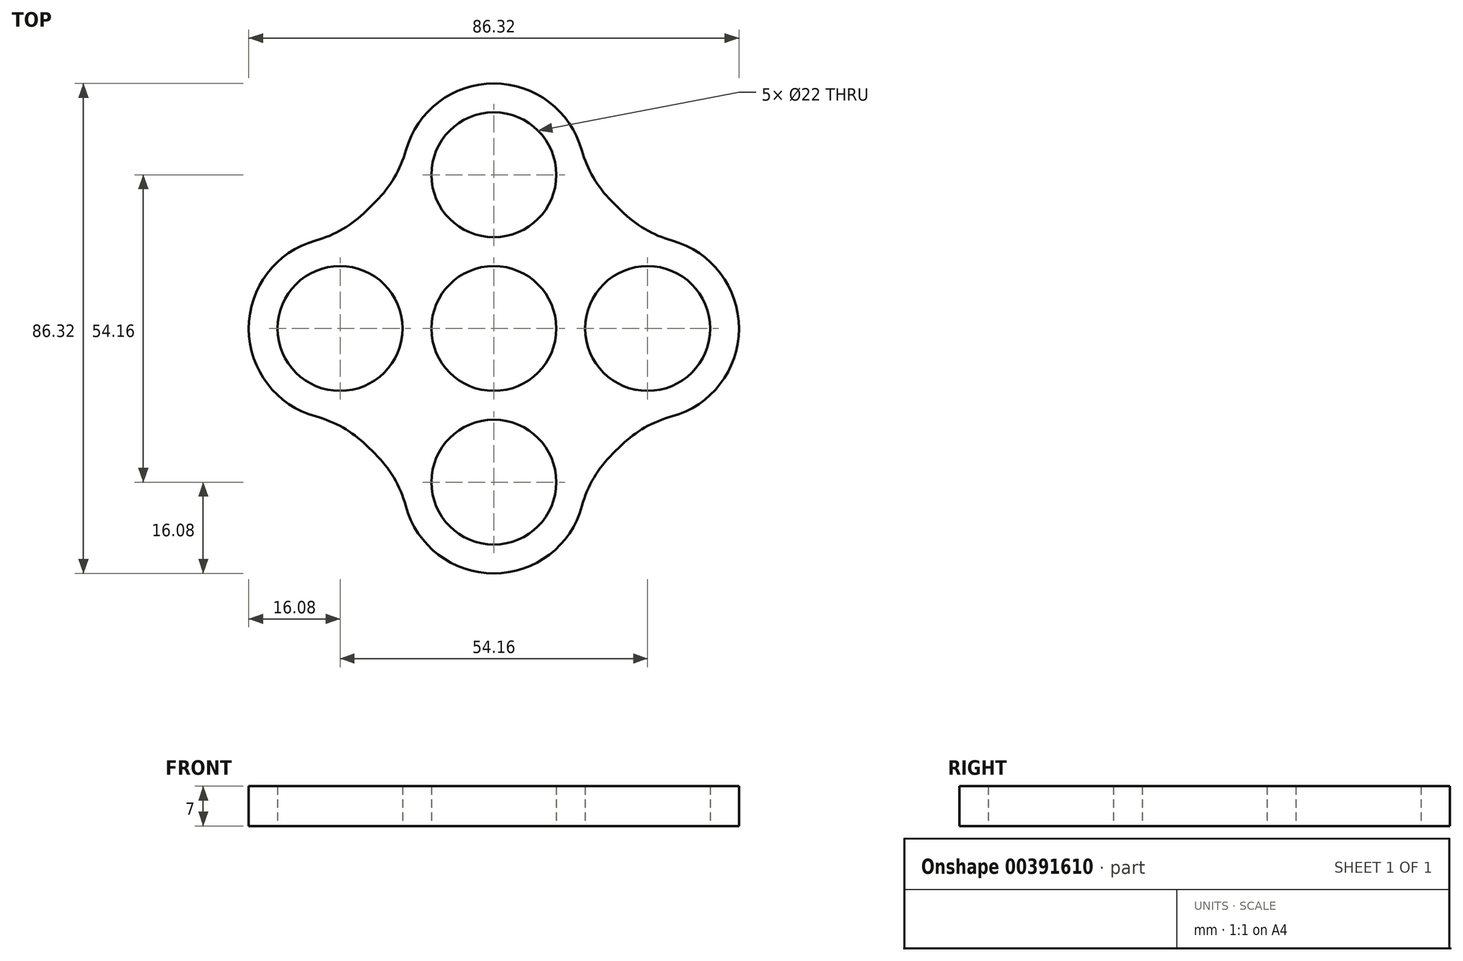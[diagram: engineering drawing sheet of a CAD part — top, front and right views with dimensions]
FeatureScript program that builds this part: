
annotation { "Feature Type Name" : "Feature", "Feature Type Description" : "" }
export const myFeature = defineFeature(function(context is Context, id is Id, definition is map)
    precondition{}
    {
        {
            var Q0;
            Q0=qCreatedBy(makeId("Top.planeOp"),FACE);
            var sketch = newSketch(context, id + "F0", { "sketchPlane" : qUnion([Q0])});
            skArc(sketch, "E0", {"start": v(0, 11) * mm, "mid": v(-11, 0) * mm, "end": v(0, -11) * mm});
            skArc(sketch, "E1", {"start": v(0, 38.08) * mm, "mid": v(-11, 27.08) * mm, "end": v(0, 16.08) * mm});
            skCircle(sketch, "E2", {"center": v(-27.08, 0) * mm, "radius": 11 * mm});
            skArc(sketch, "E3", {"start": v(0, -16.08) * mm, "mid": v(-11, -27.08) * mm, "end": v(0, -38.08) * mm});
            skLineSegment(sketch, "E4", {"start": v(0, 57.5) * mm, "end": v(0, -57.23) * mm, "construction": true});
            skArc(sketch, "E5", {"start": v(0, 43.16) * mm, "mid": v(-16.08, 27.08) * mm, "end": v(0, 11) * mm});
            skCircle(sketch, "E6", {"center": v(-27.08, 0) * mm, "radius": 16.08 * mm});
            skArc(sketch, "E7", {"start": v(0, -11) * mm, "mid": v(-16.08, -27.08) * mm, "end": v(0, -43.16) * mm});
            skLineSegment(sketch, "E8", {"start": v(-27.08, -16.08) * mm, "end": v(-16.08, -26.79) * mm});
            skPoint(sketch, "E9.endSnap0", {"position": v(-16.08, 27.08) * mm});
            skLineSegment(sketch, "E10", {"start": v(-16.08, 27.08) * mm, "end": v(-27.08, 16.08) * mm});
            skPoint(sketch, "E11.MirrorP", {"position": v(16.08, 27.08) * mm});
            skArc(sketch, "E12.MirrorCS", {"start": v(0, 43.16) * mm, "mid": v(16.08, 27.08) * mm, "end": v(0, 11) * mm});
            skArc(sketch, "E13.MirrorCS", {"start": v(0, 11) * mm, "mid": v(11, 0) * mm, "end": v(0, -11) * mm});
            skArc(sketch, "E14.MirrorCS", {"start": v(0, 38.08) * mm, "mid": v(11, 27.08) * mm, "end": v(0, 16.08) * mm});
            skArc(sketch, "E15.MirrorCS", {"start": v(0, -16.08) * mm, "mid": v(11, -27.08) * mm, "end": v(0, -38.08) * mm});
            skLineSegment(sketch, "E16.MirrorCS", {"start": v(16.08, 27.08) * mm, "end": v(27.08, 16.08) * mm});
            skCircle(sketch, "E17.MirrorC", {"center": v(27.08, 0) * mm, "radius": 16.08 * mm});
            skArc(sketch, "E18.MirrorCS", {"start": v(0, -11) * mm, "mid": v(16.08, -27.08) * mm, "end": v(0, -43.16) * mm});
            skLineSegment(sketch, "E19.MirrorCS", {"start": v(27.08, -16.08) * mm, "end": v(16.08, -26.79) * mm});
            skCircle(sketch, "E20.MirrorC", {"center": v(27.08, 0) * mm, "radius": 11 * mm});
            skSolve(sketch);
        }
        {
            var Q0;
            Q0 = qSketchRegion(id + "F0", true);
            extrude(context, id + "F1", {"entities" : qUnion([Q0]), "depth" : 7 * mm});
        }
        {
            var Q0;
            Q0=makeQuery(id+"F1.opExtrude","SWEPT_EDGE",EDGE,{"disambiguationData":[OSD([sQuery(id+"F0.wireOp",EDGE,"E5"),sQuery(id+"F0.wireOp",EDGE,"E10")])]});
            var Q1;
            Q1=makeQuery(id+"F1.opExtrude","SWEPT_EDGE",EDGE,{"disambiguationData":[OSD([sQuery(id+"F0.wireOp",EDGE,"E6"),sQuery(id+"F0.wireOp",EDGE,"E10")])]});
            var Q2;
            Q2=makeQuery(id+"F1.opExtrude","SWEPT_EDGE",EDGE,{"disambiguationData":[OSD([sQuery(id+"F0.wireOp",EDGE,"E12.MirrorCS"),sQuery(id+"F0.wireOp",EDGE,"E16.MirrorCS")])]});
            var Q3;
            Q3=makeQuery(id+"F1.opExtrude","SWEPT_EDGE",EDGE,{"disambiguationData":[OSD([sQuery(id+"F0.wireOp",EDGE,"E16.MirrorCS"),sQuery(id+"F0.wireOp",EDGE,"E17.MirrorC")])]});
            var Q4;
            Q4=makeQuery(id+"F1.opExtrude","SWEPT_EDGE",EDGE,{"disambiguationData":[OSD([sQuery(id+"F0.wireOp",EDGE,"E17.MirrorC"),sQuery(id+"F0.wireOp",EDGE,"E19.MirrorCS")])]});
            var Q5;
            Q5=makeQuery(id+"F1.opExtrude","SWEPT_EDGE",EDGE,{"disambiguationData":[OSD([sQuery(id+"F0.wireOp",EDGE,"E18.MirrorCS"),sQuery(id+"F0.wireOp",EDGE,"E19.MirrorCS")])]});
            var Q6;
            Q6=makeQuery(id+"F1.opExtrude","SWEPT_EDGE",EDGE,{"disambiguationData":[OSD([sQuery(id+"F0.wireOp",EDGE,"E6"),sQuery(id+"F0.wireOp",EDGE,"E8")])]});
            var Q7;
            Q7=makeQuery(id+"F1.opExtrude","SWEPT_EDGE",EDGE,{"disambiguationData":[OSD([sQuery(id+"F0.wireOp",EDGE,"E7"),sQuery(id+"F0.wireOp",EDGE,"E8")])]});
            fillet(context, id + "F2", {"entities" : qUnion([Q0, Q1, Q2, Q3, Q4, Q5, Q6, Q7]), "radius" : 20.32 * mm, "tangentPropagation" : true, "allowEdgeOverflow" : false});
        }
    });
